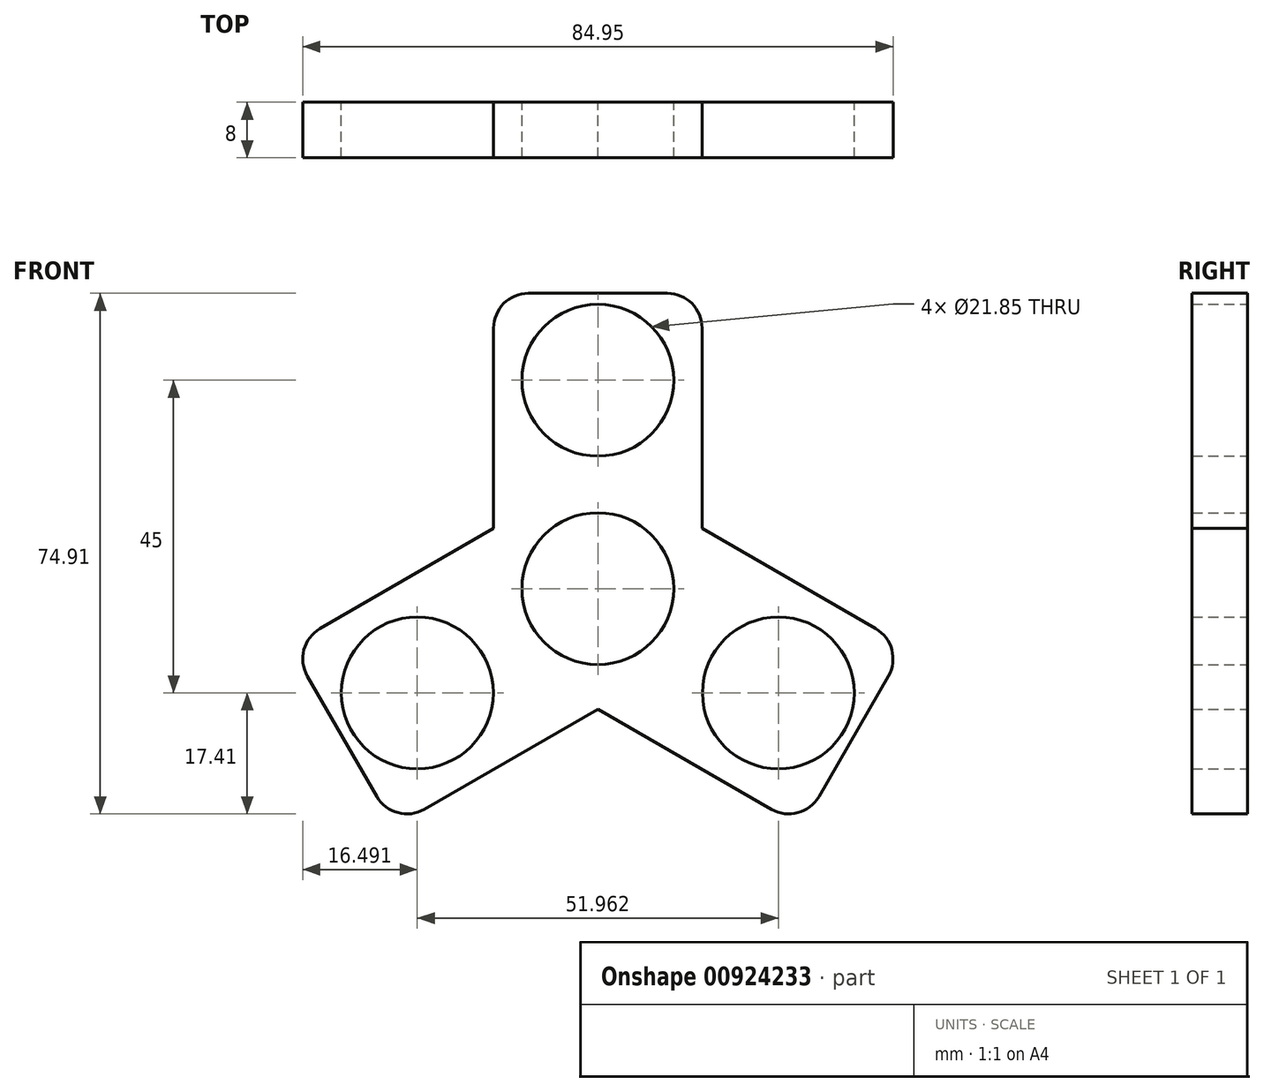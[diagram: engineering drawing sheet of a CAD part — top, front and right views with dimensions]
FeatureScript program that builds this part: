
annotation { "Feature Type Name" : "Feature", "Feature Type Description" : "" }
export const myFeature = defineFeature(function(context is Context, id is Id, definition is map)
    precondition{}
    {
        {
            var Q0;
            Q0=qCreatedBy(makeId("Front.planeOp"),FACE);
            var sketch = newSketch(context, id + "F0", { "sketchPlane" : qUnion([Q0])});
            skCircle(sketch, "E0", {"center": v(-240.8, 0) * mm, "radius": 10.92 * mm});
            skCircle(sketch, "E1", {"center": v(-240.8, 30) * mm, "radius": 10.93 * mm});
            skLineSegment(sketch, "E2", {"start": v(-240.8, 30) * mm, "end": v(-240.8, 0) * mm, "construction": true});
            skPoint(sketch, "E3", {"position": v(-240.8, 15) * mm});
            skLineSegment(sketch, "E4.bottom", {"start": v(-225.8, -12.5) * mm, "end": v(-255.8, -12.5) * mm});
            skLineSegment(sketch, "E4.top", {"start": v(-230.8, 42.5) * mm, "end": v(-250.8, 42.5) * mm});
            skLineSegment(sketch, "E4.left", {"start": v(-225.8, -12.5) * mm, "end": v(-225.8, 37.5) * mm});
            skLineSegment(sketch, "E4.right", {"start": v(-255.8, -12.5) * mm, "end": v(-255.8, 37.5) * mm});
            skPoint(sketch, "E5.visualSharp", {"position": v(-255.8, 42.5) * mm});
            skArc(sketch, "E5.filletArc", {"start": v(-250.8, 42.5) * mm, "mid": v(-254.33, 41.04) * mm, "end": v(-255.8, 37.5) * mm});
            skPoint(sketch, "E6.visualSharp", {"position": v(-225.8, 42.5) * mm});
            skArc(sketch, "E6.filletArc", {"start": v(-225.8, 37.5) * mm, "mid": v(-227.26, 41.04) * mm, "end": v(-230.8, 42.5) * mm});
            skPoint(sketch, "E7.1.0", {"position": v(-285.1, -8.26) * mm});
            skPoint(sketch, "E7.1.1", {"position": v(-270.1, -34.24) * mm});
            skLineSegment(sketch, "E7.1.2", {"start": v(-282.6, -12.59) * mm, "end": v(-272.6, -29.91) * mm});
            skLineSegment(sketch, "E7.1.3", {"start": v(-237.47, 19.24) * mm, "end": v(-280.77, -5.76) * mm});
            skLineSegment(sketch, "E7.1.5", {"start": v(-222.47, -6.74) * mm, "end": v(-265.77, -31.74) * mm});
            skLineSegment(sketch, "E7.1.6", {"start": v(-266.78, -15) * mm, "end": v(-240.8, 0) * mm, "construction": true});
            skLineSegment(sketch, "E7.1.7", {"start": v(-237.47, 19.24) * mm, "end": v(-222.47, -6.74) * mm});
            skCircle(sketch, "E7.1.8", {"center": v(-266.78, -15) * mm, "radius": 10.93 * mm});
            skPoint(sketch, "E7.1.9", {"position": v(-253.79, -7.5) * mm});
            skPoint(sketch, "E7.1.10", {"position": v(-253.79, -7.5) * mm});
            skArc(sketch, "E7.1.11", {"start": v(-280.77, -5.76) * mm, "mid": v(-283.1, -8.8) * mm, "end": v(-282.6, -12.59) * mm});
            skArc(sketch, "E7.1.12", {"start": v(-272.6, -29.91) * mm, "mid": v(-269.57, -32.24) * mm, "end": v(-265.77, -31.74) * mm});
            skPoint(sketch, "E7.2.0", {"position": v(-211.5, -34.24) * mm});
            skPoint(sketch, "E7.2.1", {"position": v(-196.5, -8.26) * mm});
            skLineSegment(sketch, "E7.2.2", {"start": v(-209, -29.91) * mm, "end": v(-199, -12.59) * mm});
            skLineSegment(sketch, "E7.2.3", {"start": v(-259.12, -6.74) * mm, "end": v(-215.82, -31.74) * mm});
            skLineSegment(sketch, "E7.2.5", {"start": v(-244.12, 19.24) * mm, "end": v(-200.82, -5.76) * mm});
            skLineSegment(sketch, "E7.2.6", {"start": v(-214.82, -15) * mm, "end": v(-240.8, 0) * mm, "construction": true});
            skLineSegment(sketch, "E7.2.7", {"start": v(-259.12, -6.74) * mm, "end": v(-244.12, 19.24) * mm});
            skCircle(sketch, "E7.2.8", {"center": v(-214.82, -15) * mm, "radius": 10.93 * mm});
            skPoint(sketch, "E7.2.9", {"position": v(-227.8, -7.5) * mm});
            skPoint(sketch, "E7.2.10", {"position": v(-227.8, -7.5) * mm});
            skArc(sketch, "E7.2.11", {"start": v(-215.82, -31.74) * mm, "mid": v(-212.03, -32.24) * mm, "end": v(-209, -29.91) * mm});
            skArc(sketch, "E7.2.12", {"start": v(-199, -12.59) * mm, "mid": v(-198.5, -8.8) * mm, "end": v(-200.82, -5.76) * mm});
            skSolve(sketch);
        }
        {
            var Q0;
            Q0 = qSketchRegion(id + "F0", true);
            var Q1;
            {var subQ0=sQuery(id+"F0.wireOp",EDGE,"E7.2.5");var subQ1=sQuery(id+"F0.wireOp",EDGE,"E7.1.3");var subQ2=makeQuery(id+"F0.imprint","INTERSECT",VERTEX,{"derivedFrom":[subQ1,subQ0]});Q1=makeQuery(id+"F0.imprint","IMPRINT",FACE,{"disambiguationData":[TD([[makeQuery(id+"F0.imprint","IMPRINT",EDGE,{"disambiguationData":[TD([[subQ2,-1.0]])],"derivedFrom":subQ1}),-1.0]])]});}
            var Q2;
            {var subQ0=sQuery(id+"F0.wireOp",EDGE,"E7.1.7");var subQ1=sQuery(id+"F0.wireOp",EDGE,"E7.1.3");var subQ2=makeQuery(id+"F0.imprint","INTERSECT",VERTEX,{"derivedFrom":[subQ1,subQ0]});Q2=makeQuery(id+"F0.imprint","IMPRINT",FACE,{"disambiguationData":[TD([[makeQuery(id+"F0.imprint","IMPRINT",EDGE,{"disambiguationData":[TD([[subQ2,-1.0]])],"derivedFrom":subQ1}),1.0]])]});}
            var Q3;
            Q3=makeQuery(id+"F0.imprint","IMPRINT",FACE,{"disambiguationData":[TD([[makeQuery(id+"F0.imprint","IMPRINT",EDGE,{"derivedFrom":sQuery(id+"F0.wireOp",EDGE,"E0")}),-1.0]])]});
            var Q4;
            {var subQ0=sQuery(id+"F0.wireOp",EDGE,"E7.1.5");var subQ1=sQuery(id+"F0.wireOp",EDGE,"E4.left");var subQ2=makeQuery(id+"F0.imprint","INTERSECT",VERTEX,{"derivedFrom":[subQ1,subQ0]});Q4=makeQuery(id+"F0.imprint","IMPRINT",FACE,{"disambiguationData":[TD([[makeQuery(id+"F0.imprint","IMPRINT",EDGE,{"disambiguationData":[TD([[subQ2,-1.0]])],"derivedFrom":subQ1}),-1.0]])]});}
            var Q5;
            {var subQ0=sQuery(id+"F0.wireOp",EDGE,"E4.left");var subQ1=sQuery(id+"F0.wireOp",EDGE,"E4.bottom");var subQ2=makeQuery(id+"F0.imprint","INTERSECT",VERTEX,{"derivedFrom":[subQ1,subQ0]});Q5=makeQuery(id+"F0.imprint","IMPRINT",FACE,{"disambiguationData":[TD([[makeQuery(id+"F0.imprint","IMPRINT",EDGE,{"disambiguationData":[TD([[subQ2,-1.0]])],"derivedFrom":subQ1}),-1.0]])]});}
            var Q6;
            {var subQ0=sQuery(id+"F0.wireOp",EDGE,"E4.right");var subQ1=sQuery(id+"F0.wireOp",EDGE,"E4.bottom");var subQ2=makeQuery(id+"F0.imprint","INTERSECT",VERTEX,{"derivedFrom":[subQ1,subQ0]});Q6=makeQuery(id+"F0.imprint","IMPRINT",FACE,{"disambiguationData":[TD([[makeQuery(id+"F0.imprint","IMPRINT",EDGE,{"disambiguationData":[TD([[subQ2,1.0]])],"derivedFrom":subQ1}),-1.0]])]});}
            var Q7;
            {var subQ0=sQuery(id+"F0.wireOp",EDGE,"E7.2.3");var subQ1=sQuery(id+"F0.wireOp",EDGE,"E4.right");var subQ2=makeQuery(id+"F0.imprint","INTERSECT",VERTEX,{"derivedFrom":[subQ1,subQ0]});Q7=makeQuery(id+"F0.imprint","IMPRINT",FACE,{"disambiguationData":[TD([[makeQuery(id+"F0.imprint","IMPRINT",EDGE,{"disambiguationData":[TD([[subQ2,-1.0]])],"derivedFrom":subQ1}),1.0]])]});}
            extrude(context, id + "F1", {"entities" : qUnion([Q0, Q1, Q2, Q3, Q4, Q5, Q6, Q7]), "depth" : 8 * mm, "offsetDistance" : 25 * mm});
        }
    });
